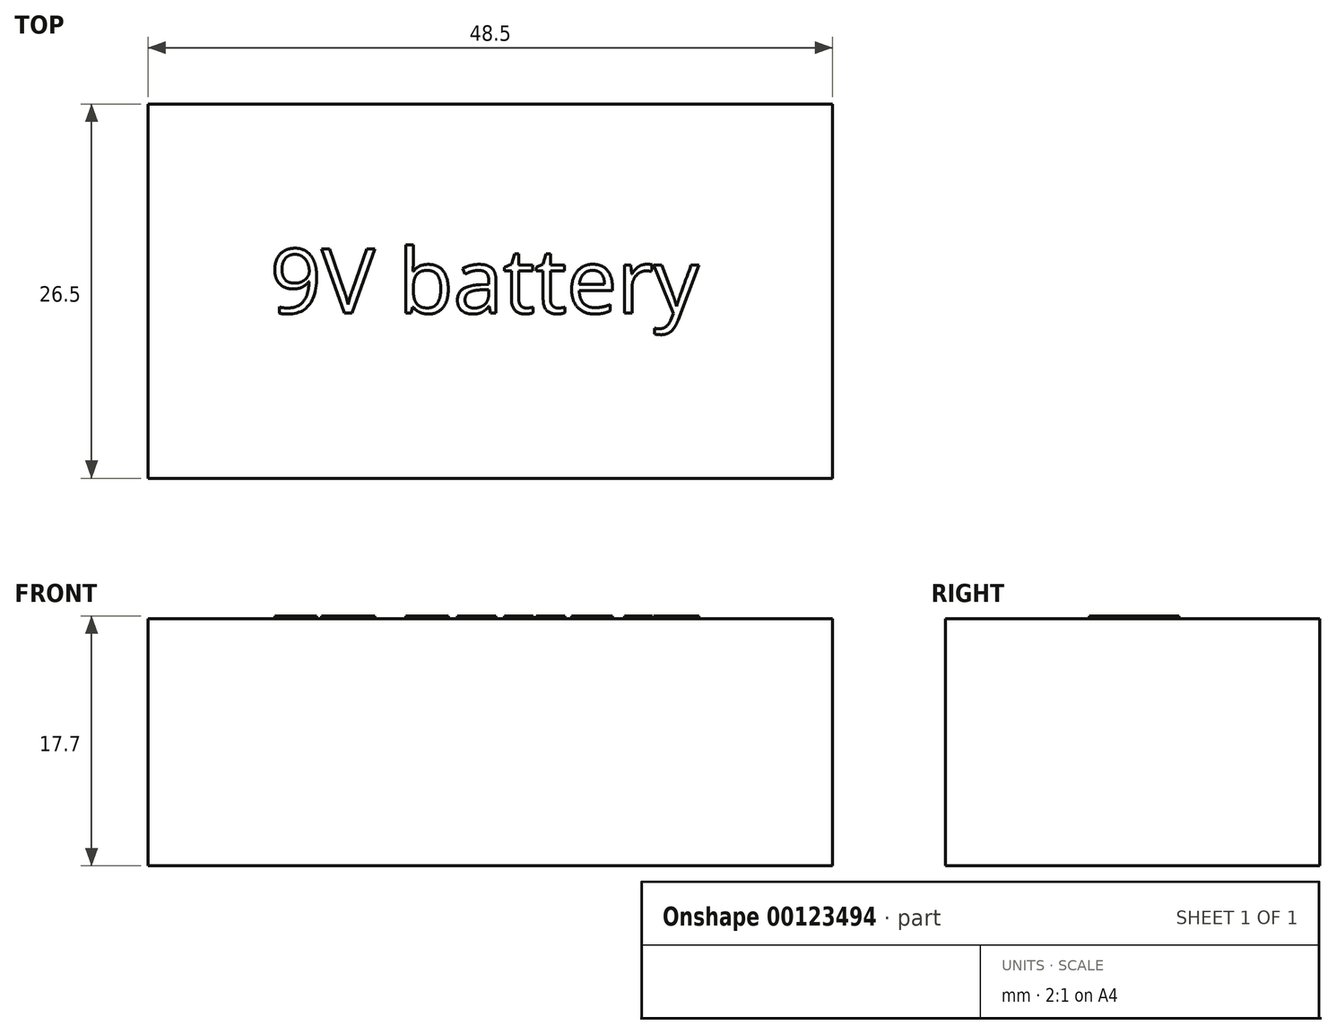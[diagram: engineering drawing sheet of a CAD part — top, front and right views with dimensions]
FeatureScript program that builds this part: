
annotation { "Feature Type Name" : "Feature", "Feature Type Description" : "" }
export const myFeature = defineFeature(function(context is Context, id is Id, definition is map)
    precondition{}
    {
        {
            var Q0;
            Q0=qCreatedBy(makeId("Top.planeOp"),FACE);
            var sketch = newSketch(context, id + "F0", { "sketchPlane" : qUnion([Q0])});
            skLineSegment(sketch, "E0.bottom", {"start": v(0, 0) * mm, "end": v(48.5, 0) * mm});
            skLineSegment(sketch, "E0.top", {"start": v(0, 26.5) * mm, "end": v(48.5, 26.5) * mm});
            skLineSegment(sketch, "E0.left", {"start": v(0, 0) * mm, "end": v(0, 26.5) * mm});
            skLineSegment(sketch, "E0.right", {"start": v(48.5, 0) * mm, "end": v(48.5, 26.5) * mm});
            skSolve(sketch);
        }
        {
            var Q0;
            Q0=makeQuery(id+"F0.imprint","IMPRINT",FACE,{"disambiguationData":[TD([[makeQuery(id+"F0.imprint","IMPRINT",EDGE,{"derivedFrom":sQuery(id+"F0.wireOp",EDGE,"E0.bottom")}),1.0]])]});
            extrude(context, id + "F1", {"entities" : qUnion([Q0]), "depth" : 17.5 * mm});
        }
        {
            var Q0;
            Q0=makeQuery(id+"F1.opExtrude","CAP_FACE",FACE,{"disambiguationData":[OSD([sQuery(id+"F0.wireOp",EDGE,"E0.bottom"),sQuery(id+"F0.wireOp",EDGE,"E0.top"),sQuery(id+"F0.wireOp",EDGE,"E0.left"),sQuery(id+"F0.wireOp",EDGE,"E0.right")])],"isStart":false});
            var sketch = newSketch(context, id + "F2", { "sketchPlane" : qUnion([Q0])});
            skText(sketch, "E1", { "text": "9V battery", "fontName": "OpenSans-Regular.ttf"});
            const initialGuessF2  = {"E1": [0.00865, 0.01169, 1, 0, 0.00458]};
            skSetInitialGuess(sketch, initialGuessF2);
            skSolve(sketch);
        }
        {
            var Q0;
            Q0 = qSketchRegion(id + "F2", true);
            extrude(context, id + "F3", {"entities" : qUnion([Q0]), "operationType" : NewBodyOperationType.ADD, "depth" : 0.2 * mm});
        }
    });
